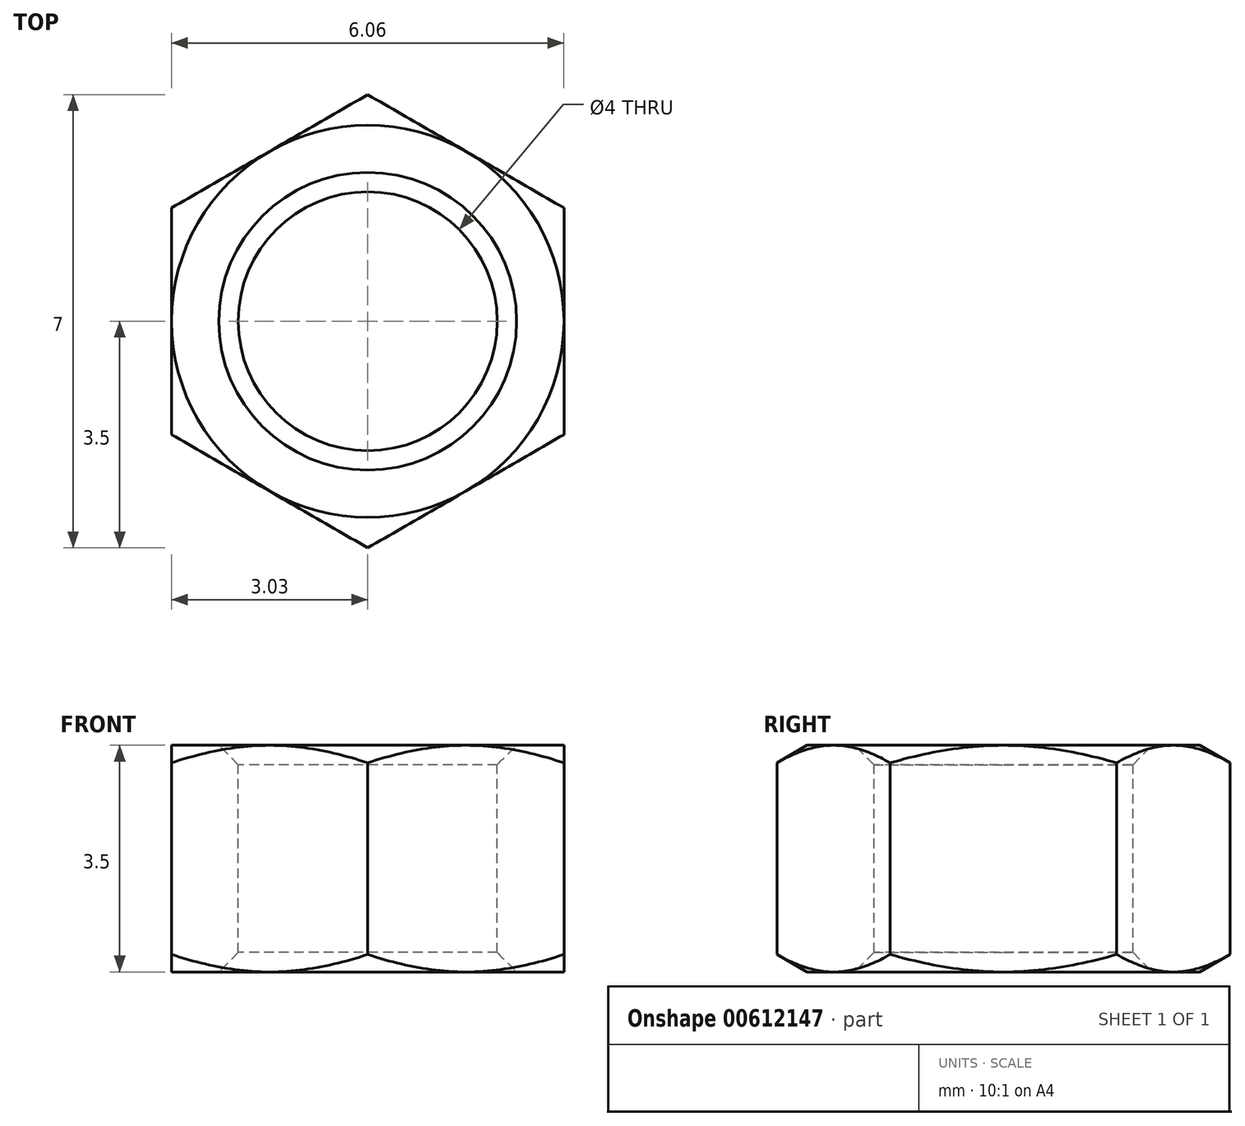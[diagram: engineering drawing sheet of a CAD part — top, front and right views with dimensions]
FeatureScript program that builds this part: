
annotation { "Feature Type Name" : "Feature", "Feature Type Description" : "" }
export const myFeature = defineFeature(function(context is Context, id is Id, definition is map)
    precondition{}
    {
        {
            var Q0;
            Q0=qCreatedBy(makeId("Top.planeOp"),FACE);
            var sketch = newSketch(context, id + "F0", { "sketchPlane" : qUnion([Q0])});
            skCircle(sketch, "E0.cCircle", {"center": v(0, 0) * mm, "radius": 3.5 * mm, "construction": true});
            skLineSegment(sketch, "E0.0", {"start": v(0, -3.5) * mm, "end": v(-3.03, -1.75) * mm});
            skLineSegment(sketch, "E0.1", {"start": v(-3.03, -1.75) * mm, "end": v(-3.03, 1.75) * mm});
            skLineSegment(sketch, "E0.2", {"start": v(-3.03, 1.75) * mm, "end": v(0, 3.5) * mm});
            skLineSegment(sketch, "E0.3", {"start": v(0, 3.5) * mm, "end": v(3.03, 1.75) * mm});
            skLineSegment(sketch, "E0.4", {"start": v(3.03, 1.75) * mm, "end": v(3.03, -1.75) * mm});
            skLineSegment(sketch, "E0.5", {"start": v(3.03, -1.75) * mm, "end": v(0, -3.5) * mm});
            skCircle(sketch, "E1", {"center": v(0, 0) * mm, "radius": 2 * mm});
            skSolve(sketch);
        }
        {
            var Q0;
            Q0 = qSketchRegion(id + "F0", true);
            extrude(context, id + "F1", {"entities" : qUnion([Q0]), "oppositeDirection" : true, "depth" : 3.5 * mm, "offsetDistance" : 25 * mm});
        }
        {
            var Q0;
            Q0=qCreatedBy(makeId("Front.planeOp"),FACE);
            var sketch = newSketch(context, id + "F2", { "sketchPlane" : qUnion([Q0])});
            skLineSegment(sketch, "E2", {"start": v(0, 0) * mm, "end": v(0, -3.5) * mm, "construction": true});
            skLineSegment(sketch, "E3", {"start": v(0, -1.75) * mm, "end": v(3.03, -1.75) * mm, "construction": true});
            skLineSegment(sketch, "E4", {"start": v(3.03, 0) * mm, "end": v(5.8, 0) * mm});
            skLineSegment(sketch, "E5", {"start": v(5.8, 0) * mm, "end": v(5.8, -1.6) * mm});
            skLineSegment(sketch, "E6", {"start": v(5.8, -1.6) * mm, "end": v(3.03, 0) * mm});
            skLineSegment(sketch, "E7.MirrorCS", {"start": v(5.8, -1.9) * mm, "end": v(3.03, -3.5) * mm});
            skLineSegment(sketch, "E8.MirrorCS", {"start": v(3.03, -3.5) * mm, "end": v(5.8, -3.5) * mm});
            skLineSegment(sketch, "E9.MirrorCS", {"start": v(5.8, -3.5) * mm, "end": v(5.8, -1.9) * mm});
            skSolve(sketch);
        }
        {
            var Q0;
            Q0=makeQuery(id+"F2.imprint","IMPRINT",FACE,{"disambiguationData":[TD([[makeQuery(id+"F2.imprint","IMPRINT",EDGE,{"derivedFrom":sQuery(id+"F2.wireOp",EDGE,"E4")}),-1.0]])]});
            var Q1;
            Q1=makeQuery(id+"F2.imprint","IMPRINT",FACE,{"disambiguationData":[TD([[makeQuery(id+"F2.imprint","IMPRINT",EDGE,{"derivedFrom":sQuery(id+"F2.wireOp",EDGE,"E7.MirrorCS")}),1.0]])]});
            var Q2;
            Q2=sQuery(id+"F2.wireOp",EDGE,"E2");
            revolve(context, id + "F3", {"operationType" : NewBodyOperationType.REMOVE, "entities" : qUnion([Q0, Q1]), "axis" : qUnion([Q2]), "revolveType" : RevolveType.FULL, "oppositeDirection" : true});
        }
        {
            var Q0;
            Q0=makeQuery(id+"F1.opExtrude","CAP_EDGE",EDGE,{"disambiguationData":[OSD([sQuery(id+"F0.wireOp",EDGE,"E1")])],"isStart":true});
            var Q1;
            Q1=makeQuery(id+"F1.opExtrude","CAP_EDGE",EDGE,{"disambiguationData":[OSD([sQuery(id+"F0.wireOp",EDGE,"E1")])],"isStart":false});
            chamfer(context, id + "F4", {"entities" : qUnion([Q0, Q1]), "width" : 0.3 * mm, "tangentPropagation" : true});
        }
    });
